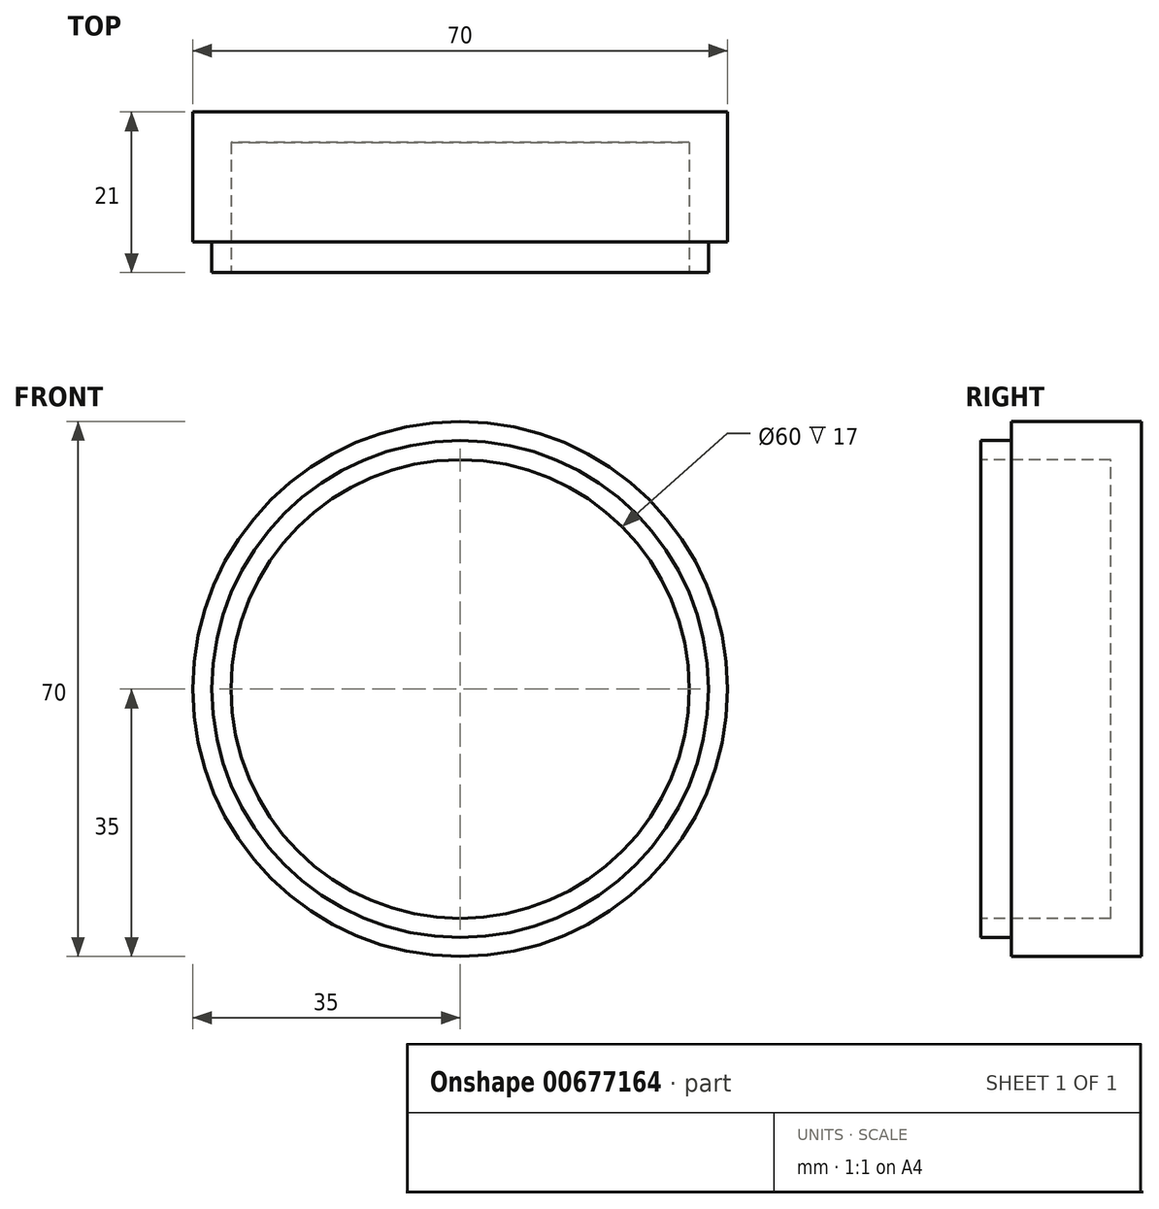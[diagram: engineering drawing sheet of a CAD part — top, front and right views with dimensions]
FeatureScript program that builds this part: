
annotation { "Feature Type Name" : "Feature", "Feature Type Description" : "" }
export const myFeature = defineFeature(function(context is Context, id is Id, definition is map)
    precondition{}
    {
        {
            var Q0;
            Q0=qCreatedBy(makeId("Front.planeOp"),FACE);
            var sketch = newSketch(context, id + "F0", { "sketchPlane" : qUnion([Q0])});
            skCircle(sketch, "E0", {"center": v(0, 0) * mm, "radius": 35 * mm});
            skSolve(sketch);
        }
        {
            var Q0;
            Q0=makeQuery(id+"F0.imprint","IMPRINT",FACE,{"disambiguationData":[TD([[makeQuery(id+"F0.imprint","IMPRINT",EDGE,{"derivedFrom":sQuery(id+"F0.wireOp",EDGE,"E0")}),1.0]])]});
            extrude(context, id + "F1", {"entities" : qUnion([Q0]), "depth" : 21 * mm, "offsetDistance" : 25 * mm});
        }
        {
            var Q0;
            Q0=makeQuery(id+"F1.opExtrude","CAP_FACE",FACE,{"disambiguationData":[OSD([sQuery(id+"F0.wireOp",EDGE,"E0")])],"isStart":false});
            var sketch = newSketch(context, id + "F2", { "sketchPlane" : qUnion([Q0])});
            skCircle(sketch, "E1", {"center": v(0, 0) * mm, "radius": 30 * mm});
            skSolve(sketch);
        }
        {
            var Q0;
            Q0=makeQuery(id+"F2.imprint","IMPRINT",FACE,{"disambiguationData":[TD([[makeQuery(id+"F2.imprint","IMPRINT",EDGE,{"derivedFrom":sQuery(id+"F2.wireOp",EDGE,"E1")}),1.0]])]});
            extrude(context, id + "F3", {"entities" : qUnion([Q0]), "operationType" : NewBodyOperationType.REMOVE, "oppositeDirection" : true, "depth" : 17 * mm, "offsetDistance" : 25 * mm});
        }
        {
            var Q0;
            Q0=makeQuery(id+"F1.opExtrude","CAP_FACE",FACE,{"disambiguationData":[OSD([sQuery(id+"F0.wireOp",EDGE,"E0")])],"isStart":false});
            var sketch = newSketch(context, id + "F4", { "sketchPlane" : qUnion([Q0])});
            skCircle(sketch, "E2", {"center": v(0, 0) * mm, "radius": 32.5 * mm});
            skSolve(sketch);
        }
        {
            var Q0;
            Q0=makeQuery(id+"F4.imprint","IMPRINT",FACE,{"disambiguationData":[TD([[makeQuery(id+"F4.imprint","IMPRINT",EDGE,{"derivedFrom":sQuery(id+"F4.wireOp",EDGE,"E2")}),-1.0]])]});
            extrude(context, id + "F5", {"entities" : qUnion([Q0]), "operationType" : NewBodyOperationType.REMOVE, "oppositeDirection" : true, "depth" : 4 * mm, "offsetDistance" : 25 * mm});
        }
    });
